# Revit family: 215x300x440mm Padstone -PS105
name_source: partatom
category: Generic Models
units: mm (PartAtom-declared; Revit-internal decimal feet)

## family parameters
Always vertical = Yes
Can host rebar = No
Cut with Voids When Loaded = No
Part Type = Normal
Room Calculation Point = No
Round Connector Dimension = Use Diameter
Shared = No
Work Plane-Based = No

## types (1)
- 215x300x440mm Padstone -PS105
    Compressive Strength of Concrete = 40N/mm²
    Construction Type = Precast
    Default Elevation = 0 mm  [stored 0 ft]
    Description = Padstone 215 x 300 x 440mm.
    Detailing = As per design specification and product drawings.
    Keynote = The information contained is the sole property of KPC Ltd., any reproduction in part or whole without permission of KPC Ltd. is prohibited.
    Length Options = Stock sizes available. Custom sizes made to order.
    Load Bearing = Yes
    Manufacturer = Killeshal Precast Concrete Ltd.
    Model = P/105 Padstone.
    Service Life = 0.000000
    Shape = As per drawing
    Size = 215 Wide x 300 High x 440mm Long.
    Slope = 0.00°
    Span = Length.
    Type Comments = Visit our website for a full list of available products.
    Types = Single
    URL = www.killeshal.com
    Weight = 68Kg

note: [stored X ft] marks values corroborated as IEEE doubles in the binary element streams (Revit-internal decimal feet)

## geometry (parser evidence)
native form markers: Sweep x3
no freeform markers — native parametric forms only
